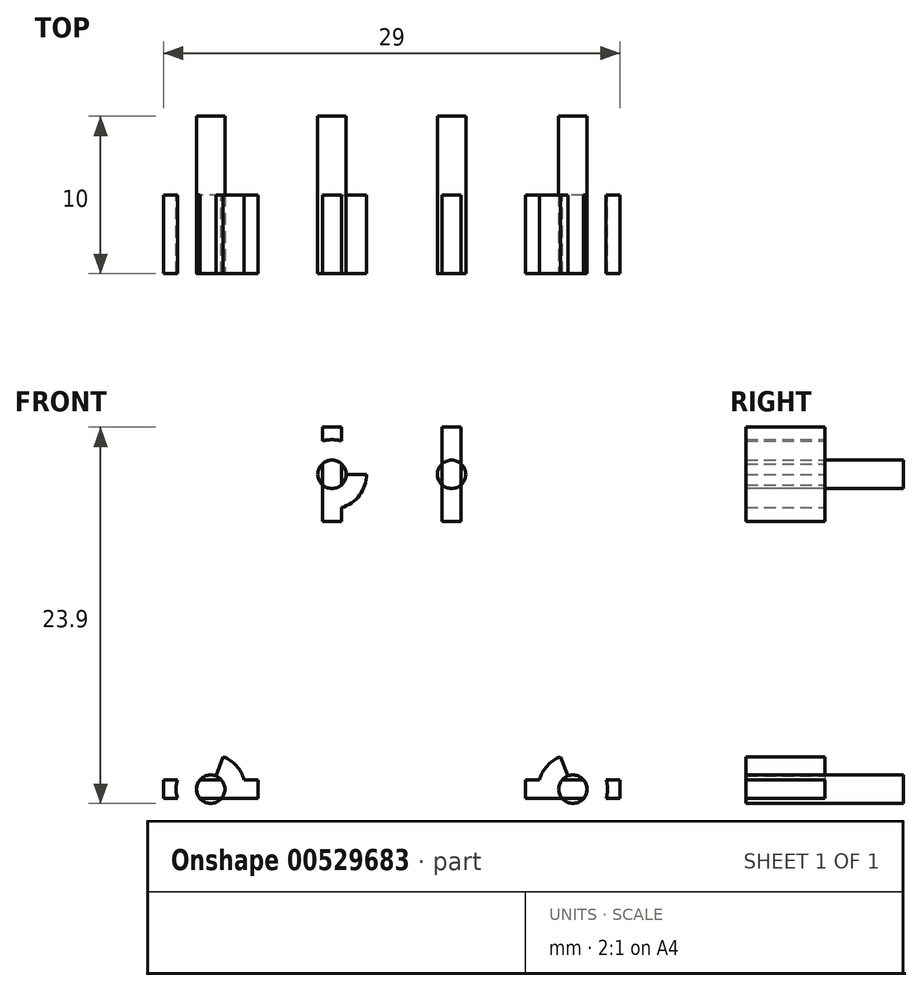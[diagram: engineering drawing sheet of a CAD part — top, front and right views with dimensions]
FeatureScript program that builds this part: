
annotation { "Feature Type Name" : "Feature", "Feature Type Description" : "" }
export const myFeature = defineFeature(function(context is Context, id is Id, definition is map)
    precondition{}
    {
        {
            var Q0;
            Q0=qCreatedBy(makeId("Front.planeOp"),FACE);
            var sketch = newSketch(context, id + "F0", { "sketchPlane" : qUnion([Q0])});
            skLineSegment(sketch, "E0", {"start": v(-3.8, 20) * mm, "end": v(3.8, 20) * mm});
            skLineSegment(sketch, "E1", {"start": v(-11.5, 0) * mm, "end": v(11.5, 0) * mm});
            skLineSegment(sketch, "E2", {"start": v(11.5, 0) * mm, "end": v(3.8, 20) * mm});
            skLineSegment(sketch, "E3", {"start": v(-3.8, 20) * mm, "end": v(-11.5, 0) * mm});
            skCircle(sketch, "E4", {"center": v(-3.8, 20) * mm, "radius": 0.9 * mm});
            skCircle(sketch, "E5", {"center": v(3.8, 20) * mm, "radius": 0.9 * mm});
            skPoint(sketch, "E6", {"position": v(0, 20) * mm});
            skPoint(sketch, "E7", {"position": v(0, 0) * mm});
            skCircle(sketch, "E8", {"center": v(-11.5, 0) * mm, "radius": 0.9 * mm});
            skCircle(sketch, "E9", {"center": v(11.5, 0) * mm, "radius": 0.9 * mm});
            skLineSegment(sketch, "E10.bottom", {"start": v(2.5, 37) * mm, "end": v(-2.5, 37) * mm});
            skLineSegment(sketch, "E10.top", {"start": v(2.5, 30) * mm, "end": v(-2.5, 30) * mm});
            skLineSegment(sketch, "E10.left", {"start": v(2.5, 37) * mm, "end": v(2.5, 30) * mm});
            skLineSegment(sketch, "E10.right", {"start": v(-2.5, 37) * mm, "end": v(-2.5, 30) * mm});
            skPoint(sketch, "E10.middle", {"position": v(0, 33.5) * mm});
            skLineSegment(sketch, "E11.bottom", {"start": v(1.25, 30) * mm, "end": v(-1.25, 30) * mm});
            skLineSegment(sketch, "E11.top", {"start": v(1.25, 35.5) * mm, "end": v(-1.25, 35.5) * mm});
            skLineSegment(sketch, "E11.left", {"start": v(1.25, 30) * mm, "end": v(1.25, 35.5) * mm});
            skLineSegment(sketch, "E11.right", {"start": v(-1.25, 30) * mm, "end": v(-1.25, 35.5) * mm});
            skPoint(sketch, "E11.middle", {"position": v(0, 32.75) * mm});
            skCircle(sketch, "E12", {"center": v(-3.8, 20) * mm, "radius": 2.2 * mm});
            skCircle(sketch, "E13", {"center": v(3.8, 20) * mm, "radius": 2.2 * mm});
            skCircle(sketch, "E14", {"center": v(11.5, 0) * mm, "radius": 2.2 * mm});
            skCircle(sketch, "E15", {"center": v(-11.5, 0) * mm, "radius": 2.2 * mm});
            skLineSegment(sketch, "E16.bottom", {"start": v(-3.2, 17) * mm, "end": v(-4.4, 17) * mm});
            skLineSegment(sketch, "E16.top", {"start": v(-3.2, 23) * mm, "end": v(-4.4, 23) * mm});
            skLineSegment(sketch, "E16.left", {"start": v(-3.2, 17) * mm, "end": v(-3.2, 23) * mm});
            skLineSegment(sketch, "E16.right", {"start": v(-4.4, 17) * mm, "end": v(-4.4, 23) * mm});
            skLineSegment(sketch, "E17.bottom", {"start": v(4.4, 17) * mm, "end": v(3.2, 17) * mm});
            skLineSegment(sketch, "E17.top", {"start": v(4.4, 23) * mm, "end": v(3.2, 23) * mm});
            skLineSegment(sketch, "E17.left", {"start": v(4.4, 17) * mm, "end": v(4.4, 23) * mm});
            skLineSegment(sketch, "E17.right", {"start": v(3.2, 17) * mm, "end": v(3.2, 23) * mm});
            skLineSegment(sketch, "E18.bottom", {"start": v(-8.5, -0.6) * mm, "end": v(-14.5, -0.6) * mm});
            skLineSegment(sketch, "E18.top", {"start": v(-8.5, 0.6) * mm, "end": v(-14.5, 0.6) * mm});
            skLineSegment(sketch, "E18.left", {"start": v(-8.5, -0.6) * mm, "end": v(-8.5, 0.6) * mm});
            skLineSegment(sketch, "E18.right", {"start": v(-14.5, -0.6) * mm, "end": v(-14.5, 0.6) * mm});
            skLineSegment(sketch, "E19.bottom", {"start": v(14.5, -0.6) * mm, "end": v(8.5, -0.6) * mm});
            skLineSegment(sketch, "E19.top", {"start": v(14.5, 0.6) * mm, "end": v(8.5, 0.6) * mm});
            skLineSegment(sketch, "E19.left", {"start": v(14.5, -0.6) * mm, "end": v(14.5, 0.6) * mm});
            skLineSegment(sketch, "E19.right", {"start": v(8.5, -0.6) * mm, "end": v(8.5, 0.6) * mm});
            skSolve(sketch);
        }
        {
            var Q0;
            {var subQ0=sQuery(id+"F0.wireOp",EDGE,"E3");var subQ1=sQuery(id+"F0.wireOp",EDGE,"E0");var subQ2=makeQuery(id+"F0.imprint","INTERSECT",VERTEX,{"derivedFrom":[subQ1,subQ0]});Q0=makeQuery(id+"F0.imprint","IMPRINT",FACE,{"disambiguationData":[TD([[makeQuery(id+"F0.imprint","IMPRINT",EDGE,{"disambiguationData":[TD([[subQ2,-1.0]])],"derivedFrom":subQ1}),1.0]])]});}
            var Q1;
            {var subQ0=sQuery(id+"F0.wireOp",EDGE,"E3");var subQ1=sQuery(id+"F0.wireOp",EDGE,"E0");var subQ2=makeQuery(id+"F0.imprint","INTERSECT",VERTEX,{"derivedFrom":[subQ1,subQ0]});Q1=makeQuery(id+"F0.imprint","IMPRINT",FACE,{"disambiguationData":[TD([[makeQuery(id+"F0.imprint","IMPRINT",EDGE,{"disambiguationData":[TD([[subQ2,-1.0]])],"derivedFrom":subQ1}),-1.0]])]});}
            var Q2;
            {var subQ0=sQuery(id+"F0.wireOp",EDGE,"E2");var subQ1=sQuery(id+"F0.wireOp",EDGE,"E0");var subQ2=makeQuery(id+"F0.imprint","INTERSECT",VERTEX,{"derivedFrom":[subQ1,subQ0]});Q2=makeQuery(id+"F0.imprint","IMPRINT",FACE,{"disambiguationData":[TD([[makeQuery(id+"F0.imprint","IMPRINT",EDGE,{"disambiguationData":[TD([[subQ2,1.0]])],"derivedFrom":subQ1}),1.0]])]});}
            var Q3;
            {var subQ0=sQuery(id+"F0.wireOp",EDGE,"E2");var subQ1=sQuery(id+"F0.wireOp",EDGE,"E0");var subQ2=makeQuery(id+"F0.imprint","INTERSECT",VERTEX,{"derivedFrom":[subQ1,subQ0]});Q3=makeQuery(id+"F0.imprint","IMPRINT",FACE,{"disambiguationData":[TD([[makeQuery(id+"F0.imprint","IMPRINT",EDGE,{"disambiguationData":[TD([[subQ2,1.0]])],"derivedFrom":subQ1}),-1.0]])]});}
            var Q4;
            {var subQ0=sQuery(id+"F0.wireOp",EDGE,"E3");var subQ1=sQuery(id+"F0.wireOp",EDGE,"E1");var subQ2=makeQuery(id+"F0.imprint","INTERSECT",VERTEX,{"derivedFrom":[subQ1,subQ0]});Q4=makeQuery(id+"F0.imprint","IMPRINT",FACE,{"disambiguationData":[TD([[makeQuery(id+"F0.imprint","IMPRINT",EDGE,{"disambiguationData":[TD([[subQ2,-1.0]])],"derivedFrom":subQ1}),-1.0]])]});}
            var Q5;
            {var subQ0=sQuery(id+"F0.wireOp",EDGE,"E3");var subQ1=sQuery(id+"F0.wireOp",EDGE,"E1");var subQ2=makeQuery(id+"F0.imprint","INTERSECT",VERTEX,{"derivedFrom":[subQ1,subQ0]});Q5=makeQuery(id+"F0.imprint","IMPRINT",FACE,{"disambiguationData":[TD([[makeQuery(id+"F0.imprint","IMPRINT",EDGE,{"disambiguationData":[TD([[subQ2,-1.0]])],"derivedFrom":subQ1}),1.0]])]});}
            var Q6;
            {var subQ0=sQuery(id+"F0.wireOp",EDGE,"E2");var subQ1=sQuery(id+"F0.wireOp",EDGE,"E1");var subQ2=makeQuery(id+"F0.imprint","INTERSECT",VERTEX,{"derivedFrom":[subQ1,subQ0]});Q6=makeQuery(id+"F0.imprint","IMPRINT",FACE,{"disambiguationData":[TD([[makeQuery(id+"F0.imprint","IMPRINT",EDGE,{"disambiguationData":[TD([[subQ2,1.0]])],"derivedFrom":subQ1}),-1.0]])]});}
            var Q7;
            {var subQ0=sQuery(id+"F0.wireOp",EDGE,"E2");var subQ1=sQuery(id+"F0.wireOp",EDGE,"E1");var subQ2=makeQuery(id+"F0.imprint","INTERSECT",VERTEX,{"derivedFrom":[subQ1,subQ0]});Q7=makeQuery(id+"F0.imprint","IMPRINT",FACE,{"disambiguationData":[TD([[makeQuery(id+"F0.imprint","IMPRINT",EDGE,{"disambiguationData":[TD([[subQ2,1.0]])],"derivedFrom":subQ1}),1.0]])]});}
            var Q8;
            {var subQ0=sQuery(id+"F0.wireOp",EDGE,"E17.left");var subQ1=sQuery(id+"F0.wireOp",EDGE,"E5");var subQ2=makeQuery(id+"F0.imprint","INTERSECT",VERTEX,{"disambiguationData":[OD(0.0)],"derivedFrom":[subQ1,subQ0]});Q8=makeQuery(id+"F0.imprint","IMPRINT",FACE,{"disambiguationData":[TD([[makeQuery(id+"F0.imprint","IMPRINT",EDGE,{"disambiguationData":[TD([[subQ2,1.0]])],"derivedFrom":subQ1}),1.0]])]});}
            var Q9;
            {var subQ0=sQuery(id+"F0.wireOp",EDGE,"E5");var subQ1=sQuery(id+"F0.wireOp",EDGE,"E0");var subQ2=makeQuery(id+"F0.imprint","INTERSECT",VERTEX,{"derivedFrom":[subQ1,subQ0]});Q9=makeQuery(id+"F0.imprint","IMPRINT",FACE,{"disambiguationData":[TD([[makeQuery(id+"F0.imprint","IMPRINT",EDGE,{"disambiguationData":[TD([[subQ2,-1.0]])],"derivedFrom":subQ1}),1.0]])]});}
            var Q10;
            {var subQ0=sQuery(id+"F0.wireOp",EDGE,"E5");var subQ1=sQuery(id+"F0.wireOp",EDGE,"E0");var subQ2=makeQuery(id+"F0.imprint","INTERSECT",VERTEX,{"derivedFrom":[subQ1,subQ0]});Q10=makeQuery(id+"F0.imprint","IMPRINT",FACE,{"disambiguationData":[TD([[makeQuery(id+"F0.imprint","IMPRINT",EDGE,{"disambiguationData":[TD([[subQ2,-1.0]])],"derivedFrom":subQ1}),-1.0]])]});}
            var Q11;
            {var subQ0=sQuery(id+"F0.wireOp",EDGE,"E16.right");var subQ1=sQuery(id+"F0.wireOp",EDGE,"E4");var subQ2=makeQuery(id+"F0.imprint","INTERSECT",VERTEX,{"disambiguationData":[OD(0.0)],"derivedFrom":[subQ1,subQ0]});Q11=makeQuery(id+"F0.imprint","IMPRINT",FACE,{"disambiguationData":[TD([[makeQuery(id+"F0.imprint","IMPRINT",EDGE,{"disambiguationData":[TD([[subQ2,-1.0]])],"derivedFrom":subQ1}),1.0]])]});}
            var Q12;
            {var subQ0=sQuery(id+"F0.wireOp",EDGE,"E16.left");var subQ1=sQuery(id+"F0.wireOp",EDGE,"E0");var subQ2=makeQuery(id+"F0.imprint","INTERSECT",VERTEX,{"derivedFrom":[subQ1,subQ0]});Q12=makeQuery(id+"F0.imprint","IMPRINT",FACE,{"disambiguationData":[TD([[makeQuery(id+"F0.imprint","IMPRINT",EDGE,{"disambiguationData":[TD([[subQ2,-1.0]])],"derivedFrom":subQ1}),1.0]])]});}
            var Q13;
            {var subQ0=sQuery(id+"F0.wireOp",EDGE,"E16.left");var subQ1=sQuery(id+"F0.wireOp",EDGE,"E0");var subQ2=makeQuery(id+"F0.imprint","INTERSECT",VERTEX,{"derivedFrom":[subQ1,subQ0]});Q13=makeQuery(id+"F0.imprint","IMPRINT",FACE,{"disambiguationData":[TD([[makeQuery(id+"F0.imprint","IMPRINT",EDGE,{"disambiguationData":[TD([[subQ2,-1.0]])],"derivedFrom":subQ1}),-1.0]])]});}
            var Q14;
            {var subQ0=sQuery(id+"F0.wireOp",EDGE,"E18.bottom");var subQ1=sQuery(id+"F0.wireOp",EDGE,"E8");var subQ2=makeQuery(id+"F0.imprint","INTERSECT",VERTEX,{"disambiguationData":[OD(0.0)],"derivedFrom":[subQ1,subQ0]});Q14=makeQuery(id+"F0.imprint","IMPRINT",FACE,{"disambiguationData":[TD([[makeQuery(id+"F0.imprint","IMPRINT",EDGE,{"disambiguationData":[TD([[subQ2,-1.0]])],"derivedFrom":subQ1}),1.0]])]});}
            var Q15;
            {var subQ0=sQuery(id+"F0.wireOp",EDGE,"E8");var subQ1=sQuery(id+"F0.wireOp",EDGE,"E3");var subQ2=makeQuery(id+"F0.imprint","INTERSECT",VERTEX,{"derivedFrom":[subQ1,subQ0]});Q15=makeQuery(id+"F0.imprint","IMPRINT",FACE,{"disambiguationData":[TD([[makeQuery(id+"F0.imprint","IMPRINT",EDGE,{"disambiguationData":[TD([[subQ2,-1.0]])],"derivedFrom":subQ1}),-1.0]])]});}
            var Q16;
            {var subQ0=sQuery(id+"F0.wireOp",EDGE,"E8");var subQ1=sQuery(id+"F0.wireOp",EDGE,"E3");var subQ2=makeQuery(id+"F0.imprint","INTERSECT",VERTEX,{"derivedFrom":[subQ1,subQ0]});Q16=makeQuery(id+"F0.imprint","IMPRINT",FACE,{"disambiguationData":[TD([[makeQuery(id+"F0.imprint","IMPRINT",EDGE,{"disambiguationData":[TD([[subQ2,-1.0]])],"derivedFrom":subQ1}),1.0]])]});}
            var Q17;
            {var subQ0=sQuery(id+"F0.wireOp",EDGE,"E19.top");var subQ1=sQuery(id+"F0.wireOp",EDGE,"E2");var subQ2=makeQuery(id+"F0.imprint","INTERSECT",VERTEX,{"derivedFrom":[subQ1,subQ0]});Q17=makeQuery(id+"F0.imprint","IMPRINT",FACE,{"disambiguationData":[TD([[makeQuery(id+"F0.imprint","IMPRINT",EDGE,{"disambiguationData":[TD([[subQ2,-1.0]])],"derivedFrom":subQ1}),-1.0]])]});}
            var Q18;
            {var subQ0=sQuery(id+"F0.wireOp",EDGE,"E19.top");var subQ1=sQuery(id+"F0.wireOp",EDGE,"E2");var subQ2=makeQuery(id+"F0.imprint","INTERSECT",VERTEX,{"derivedFrom":[subQ1,subQ0]});Q18=makeQuery(id+"F0.imprint","IMPRINT",FACE,{"disambiguationData":[TD([[makeQuery(id+"F0.imprint","IMPRINT",EDGE,{"disambiguationData":[TD([[subQ2,-1.0]])],"derivedFrom":subQ1}),1.0]])]});}
            var Q19;
            {var subQ0=sQuery(id+"F0.wireOp",EDGE,"E19.bottom");var subQ1=sQuery(id+"F0.wireOp",EDGE,"E9");var subQ2=makeQuery(id+"F0.imprint","INTERSECT",VERTEX,{"disambiguationData":[OD(0.0)],"derivedFrom":[subQ1,subQ0]});Q19=makeQuery(id+"F0.imprint","IMPRINT",FACE,{"disambiguationData":[TD([[makeQuery(id+"F0.imprint","IMPRINT",EDGE,{"disambiguationData":[TD([[subQ2,-1.0]])],"derivedFrom":subQ1}),1.0]])]});}
            var Q20;
            Q20=sQuery(id+"F0.wireOp",EDGE,"E4");
            var Q21;
            Q21=sQuery(id+"F0.wireOp",EDGE,"E5");
            extrude(context, id + "F1", {"entities" : qUnion([Q0, Q1, Q2, Q3, Q4, Q5, Q6, Q7, Q8, Q9, Q10, Q11, Q12, Q13, Q14, Q15, Q16, Q17, Q18, Q19]), "surfaceEntities" : qUnion([Q20, Q21]), "oppositeDirection" : true, "depth" : 5 * mm, "offsetDistance" : 25 * mm, "hasSecondDirection" : true, "secondDirectionOppositeDirection" : false, "secondDirectionDepth" : 5 * mm});
        }
        {
            var Q0;
            {var subQ5=sQuery(id+"F0.wireOp",EDGE,"E18.right");Q0=makeQuery(id+"F0.imprint","IMPRINT",FACE,{"disambiguationData":[TD([[makeQuery(id+"F0.imprint","IMPRINT",EDGE,{"derivedFrom":subQ5}),-1.0]])]});}
            var Q1;
            {var subQ0=sQuery(id+"F0.wireOp",EDGE,"E18.top");var subQ1=sQuery(id+"F0.wireOp",EDGE,"E8");var subQ2=makeQuery(id+"F0.imprint","INTERSECT",VERTEX,{"disambiguationData":[OD(1.0)],"derivedFrom":[subQ1,subQ0]});Q1=makeQuery(id+"F0.imprint","IMPRINT",FACE,{"disambiguationData":[TD([[makeQuery(id+"F0.imprint","IMPRINT",EDGE,{"disambiguationData":[TD([[subQ2,-1.0]])],"derivedFrom":subQ1}),-1.0]])]});}
            var Q2;
            {var subQ1=sQuery(id+"F0.wireOp",EDGE,"E1");var subQ8=sQuery(id+"F0.wireOp",EDGE,"E3");var subQ9=makeQuery(id+"F0.imprint","INTERSECT",VERTEX,{"derivedFrom":[subQ1,subQ8]});Q2=makeQuery(id+"F0.imprint","IMPRINT",FACE,{"disambiguationData":[TD([[makeQuery(id+"F0.imprint","IMPRINT",EDGE,{"disambiguationData":[TD([[subQ9,-1.0]])],"derivedFrom":subQ1}),-1.0]])]});}
            var Q3;
            {var subQ0=sQuery(id+"F0.wireOp",EDGE,"E8");var subQ1=sQuery(id+"F0.wireOp",EDGE,"E1");var subQ2=makeQuery(id+"F0.imprint","INTERSECT",VERTEX,{"derivedFrom":[subQ1,subQ0]});Q3=makeQuery(id+"F0.imprint","IMPRINT",FACE,{"disambiguationData":[TD([[makeQuery(id+"F0.imprint","IMPRINT",EDGE,{"disambiguationData":[TD([[subQ2,-1.0]])],"derivedFrom":subQ1}),1.0]])]});}
            var Q4;
            {var subQ0=sQuery(id+"F0.wireOp",EDGE,"E8");var subQ1=sQuery(id+"F0.wireOp",EDGE,"E1");var subQ2=makeQuery(id+"F0.imprint","INTERSECT",VERTEX,{"derivedFrom":[subQ1,subQ0]});Q4=makeQuery(id+"F0.imprint","IMPRINT",FACE,{"disambiguationData":[TD([[makeQuery(id+"F0.imprint","IMPRINT",EDGE,{"disambiguationData":[TD([[subQ2,-1.0]])],"derivedFrom":subQ1}),-1.0]])]});}
            var Q5;
            {var subQ0=sQuery(id+"F0.wireOp",EDGE,"E18.left");var subQ1=sQuery(id+"F0.wireOp",EDGE,"E1");var subQ2=makeQuery(id+"F0.imprint","INTERSECT",VERTEX,{"derivedFrom":[subQ1,subQ0]});Q5=makeQuery(id+"F0.imprint","IMPRINT",FACE,{"disambiguationData":[TD([[makeQuery(id+"F0.imprint","IMPRINT",EDGE,{"disambiguationData":[TD([[subQ2,1.0]])],"derivedFrom":subQ1}),-1.0]])]});}
            var Q6;
            {var subQ0=sQuery(id+"F0.wireOp",EDGE,"E18.left");var subQ1=sQuery(id+"F0.wireOp",EDGE,"E1");var subQ2=makeQuery(id+"F0.imprint","INTERSECT",VERTEX,{"derivedFrom":[subQ1,subQ0]});Q6=makeQuery(id+"F0.imprint","IMPRINT",FACE,{"disambiguationData":[TD([[makeQuery(id+"F0.imprint","IMPRINT",EDGE,{"disambiguationData":[TD([[subQ2,1.0]])],"derivedFrom":subQ1}),1.0]])]});}
            var Q7;
            {var subQ0=sQuery(id+"F0.wireOp",EDGE,"E3");var subQ1=sQuery(id+"F0.wireOp",EDGE,"E1");var subQ2=makeQuery(id+"F0.imprint","INTERSECT",VERTEX,{"derivedFrom":[subQ1,subQ0]});Q7=makeQuery(id+"F0.imprint","IMPRINT",FACE,{"disambiguationData":[TD([[makeQuery(id+"F0.imprint","IMPRINT",EDGE,{"disambiguationData":[TD([[subQ2,-1.0]])],"derivedFrom":subQ1}),1.0]])]});}
            var Q8;
            {var subQ0=sQuery(id+"F0.wireOp",EDGE,"E19.right");var subQ1=sQuery(id+"F0.wireOp",EDGE,"E1");var subQ2=makeQuery(id+"F0.imprint","INTERSECT",VERTEX,{"derivedFrom":[subQ1,subQ0]});Q8=makeQuery(id+"F0.imprint","IMPRINT",FACE,{"disambiguationData":[TD([[makeQuery(id+"F0.imprint","IMPRINT",EDGE,{"disambiguationData":[TD([[subQ2,-1.0]])],"derivedFrom":subQ1}),1.0]])]});}
            var Q9;
            {var subQ0=sQuery(id+"F0.wireOp",EDGE,"E19.right");var subQ1=sQuery(id+"F0.wireOp",EDGE,"E1");var subQ2=makeQuery(id+"F0.imprint","INTERSECT",VERTEX,{"derivedFrom":[subQ1,subQ0]});Q9=makeQuery(id+"F0.imprint","IMPRINT",FACE,{"disambiguationData":[TD([[makeQuery(id+"F0.imprint","IMPRINT",EDGE,{"disambiguationData":[TD([[subQ2,-1.0]])],"derivedFrom":subQ1}),-1.0]])]});}
            var Q10;
            {var subQ0=sQuery(id+"F0.wireOp",EDGE,"E14");var subQ1=sQuery(id+"F0.wireOp",EDGE,"E1");var subQ2=makeQuery(id+"F0.imprint","INTERSECT",VERTEX,{"derivedFrom":[subQ1,subQ0]});Q10=makeQuery(id+"F0.imprint","IMPRINT",FACE,{"disambiguationData":[TD([[makeQuery(id+"F0.imprint","IMPRINT",EDGE,{"disambiguationData":[TD([[subQ2,-1.0]])],"derivedFrom":subQ1}),-1.0]])]});}
            var Q11;
            {var subQ0=sQuery(id+"F0.wireOp",EDGE,"E14");var subQ1=sQuery(id+"F0.wireOp",EDGE,"E1");var subQ2=makeQuery(id+"F0.imprint","INTERSECT",VERTEX,{"derivedFrom":[subQ1,subQ0]});Q11=makeQuery(id+"F0.imprint","IMPRINT",FACE,{"disambiguationData":[TD([[makeQuery(id+"F0.imprint","IMPRINT",EDGE,{"disambiguationData":[TD([[subQ2,-1.0]])],"derivedFrom":subQ1}),1.0]])]});}
            var Q12;
            {var subQ0=sQuery(id+"F0.wireOp",EDGE,"E2");var subQ1=sQuery(id+"F0.wireOp",EDGE,"E1");var subQ2=makeQuery(id+"F0.imprint","INTERSECT",VERTEX,{"derivedFrom":[subQ1,subQ0]});Q12=makeQuery(id+"F0.imprint","IMPRINT",FACE,{"disambiguationData":[TD([[makeQuery(id+"F0.imprint","IMPRINT",EDGE,{"disambiguationData":[TD([[subQ2,1.0]])],"derivedFrom":subQ1}),1.0]])]});}
            var Q13;
            {var subQ5=sQuery(id+"F0.wireOp",EDGE,"E1");var subQ8=sQuery(id+"F0.wireOp",EDGE,"E2");var subQ9=makeQuery(id+"F0.imprint","INTERSECT",VERTEX,{"derivedFrom":[subQ5,subQ8]});Q13=makeQuery(id+"F0.imprint","IMPRINT",FACE,{"disambiguationData":[TD([[makeQuery(id+"F0.imprint","IMPRINT",EDGE,{"disambiguationData":[TD([[subQ9,1.0]])],"derivedFrom":subQ5}),-1.0]])]});}
            var Q14;
            {var subQ0=sQuery(id+"F0.wireOp",EDGE,"E19.top");var subQ1=sQuery(id+"F0.wireOp",EDGE,"E9");var subQ2=makeQuery(id+"F0.imprint","INTERSECT",VERTEX,{"disambiguationData":[OD(0.0)],"derivedFrom":[subQ1,subQ0]});Q14=makeQuery(id+"F0.imprint","IMPRINT",FACE,{"disambiguationData":[TD([[makeQuery(id+"F0.imprint","IMPRINT",EDGE,{"disambiguationData":[TD([[subQ2,1.0]])],"derivedFrom":subQ1}),-1.0]])]});}
            var Q15;
            {var subQ5=sQuery(id+"F0.wireOp",EDGE,"E19.left");Q15=makeQuery(id+"F0.imprint","IMPRINT",FACE,{"disambiguationData":[TD([[makeQuery(id+"F0.imprint","IMPRINT",EDGE,{"derivedFrom":subQ5}),1.0]])]});}
            var Q16;
            {var subQ5=sQuery(id+"F0.wireOp",EDGE,"E17.bottom");Q16=makeQuery(id+"F0.imprint","IMPRINT",FACE,{"disambiguationData":[TD([[makeQuery(id+"F0.imprint","IMPRINT",EDGE,{"derivedFrom":subQ5}),-1.0]])]});}
            var Q17;
            {var subQ3=sQuery(id+"F0.wireOp",EDGE,"E17.left");var subQ6=sQuery(id+"F0.wireOp",EDGE,"E2");var subQ9=makeQuery(id+"F0.imprint","INTERSECT",VERTEX,{"derivedFrom":[subQ6,subQ3]});Q17=makeQuery(id+"F0.imprint","IMPRINT",FACE,{"disambiguationData":[TD([[makeQuery(id+"F0.imprint","IMPRINT",EDGE,{"disambiguationData":[TD([[subQ9,-1.0]])],"derivedFrom":subQ6}),1.0]])]});}
            var Q18;
            {var subQ0=sQuery(id+"F0.wireOp",EDGE,"E2");var subQ1=sQuery(id+"F0.wireOp",EDGE,"E0");var subQ2=makeQuery(id+"F0.imprint","INTERSECT",VERTEX,{"derivedFrom":[subQ1,subQ0]});Q18=makeQuery(id+"F0.imprint","IMPRINT",FACE,{"disambiguationData":[TD([[makeQuery(id+"F0.imprint","IMPRINT",EDGE,{"disambiguationData":[TD([[subQ2,1.0]])],"derivedFrom":subQ1}),-1.0]])]});}
            var Q19;
            {var subQ0=sQuery(id+"F0.wireOp",EDGE,"E17.left");var subQ1=sQuery(id+"F0.wireOp",EDGE,"E2");var subQ2=makeQuery(id+"F0.imprint","INTERSECT",VERTEX,{"derivedFrom":[subQ1,subQ0]});Q19=makeQuery(id+"F0.imprint","IMPRINT",FACE,{"disambiguationData":[TD([[makeQuery(id+"F0.imprint","IMPRINT",EDGE,{"disambiguationData":[TD([[subQ2,-1.0]])],"derivedFrom":subQ1}),-1.0]])]});}
            var Q20;
            {var subQ1=sQuery(id+"F0.wireOp",EDGE,"E2");var subQ8=sQuery(id+"F0.wireOp",EDGE,"E0");var subQ9=makeQuery(id+"F0.imprint","INTERSECT",VERTEX,{"derivedFrom":[subQ8,subQ1]});Q20=makeQuery(id+"F0.imprint","IMPRINT",FACE,{"disambiguationData":[TD([[makeQuery(id+"F0.imprint","IMPRINT",EDGE,{"disambiguationData":[TD([[subQ9,1.0]])],"derivedFrom":subQ8}),1.0]])]});}
            var Q21;
            {var subQ0=sQuery(id+"F0.wireOp",EDGE,"E17.right");var subQ1=sQuery(id+"F0.wireOp",EDGE,"E5");var subQ2=makeQuery(id+"F0.imprint","INTERSECT",VERTEX,{"disambiguationData":[OD(0.0)],"derivedFrom":[subQ1,subQ0]});Q21=makeQuery(id+"F0.imprint","IMPRINT",FACE,{"disambiguationData":[TD([[makeQuery(id+"F0.imprint","IMPRINT",EDGE,{"disambiguationData":[TD([[subQ2,1.0]])],"derivedFrom":subQ1}),-1.0]])]});}
            var Q22;
            {var subQ5=sQuery(id+"F0.wireOp",EDGE,"E17.top");Q22=makeQuery(id+"F0.imprint","IMPRINT",FACE,{"disambiguationData":[TD([[makeQuery(id+"F0.imprint","IMPRINT",EDGE,{"derivedFrom":subQ5}),1.0]])]});}
            var Q23;
            {var subQ1=sQuery(id+"F0.wireOp",EDGE,"E4");var subQ5=sQuery(id+"F0.wireOp",EDGE,"E3");var subQ6=makeQuery(id+"F0.imprint","INTERSECT",VERTEX,{"derivedFrom":[subQ5,subQ1]});Q23=makeQuery(id+"F0.imprint","IMPRINT",FACE,{"disambiguationData":[TD([[makeQuery(id+"F0.imprint","IMPRINT",EDGE,{"disambiguationData":[TD([[subQ6,-1.0]])],"derivedFrom":subQ5}),1.0]])]});}
            var Q24;
            {var subQ5=sQuery(id+"F0.wireOp",EDGE,"E16.bottom");Q24=makeQuery(id+"F0.imprint","IMPRINT",FACE,{"disambiguationData":[TD([[makeQuery(id+"F0.imprint","IMPRINT",EDGE,{"derivedFrom":subQ5}),-1.0]])]});}
            var Q25;
            {var subQ0=sQuery(id+"F0.wireOp",EDGE,"E4");var subQ1=sQuery(id+"F0.wireOp",EDGE,"E3");var subQ2=makeQuery(id+"F0.imprint","INTERSECT",VERTEX,{"derivedFrom":[subQ1,subQ0]});Q25=makeQuery(id+"F0.imprint","IMPRINT",FACE,{"disambiguationData":[TD([[makeQuery(id+"F0.imprint","IMPRINT",EDGE,{"disambiguationData":[TD([[subQ2,-1.0]])],"derivedFrom":subQ1}),-1.0]])]});}
            var Q26;
            {var subQ5=sQuery(id+"F0.wireOp",EDGE,"E3");var subQ8=sQuery(id+"F0.wireOp",EDGE,"E0");var subQ9=makeQuery(id+"F0.imprint","INTERSECT",VERTEX,{"derivedFrom":[subQ8,subQ5]});Q26=makeQuery(id+"F0.imprint","IMPRINT",FACE,{"disambiguationData":[TD([[makeQuery(id+"F0.imprint","IMPRINT",EDGE,{"disambiguationData":[TD([[subQ9,-1.0]])],"derivedFrom":subQ8}),1.0]])]});}
            var Q27;
            {var subQ0=sQuery(id+"F0.wireOp",EDGE,"E3");var subQ1=sQuery(id+"F0.wireOp",EDGE,"E0");var subQ2=makeQuery(id+"F0.imprint","INTERSECT",VERTEX,{"derivedFrom":[subQ1,subQ0]});Q27=makeQuery(id+"F0.imprint","IMPRINT",FACE,{"disambiguationData":[TD([[makeQuery(id+"F0.imprint","IMPRINT",EDGE,{"disambiguationData":[TD([[subQ2,-1.0]])],"derivedFrom":subQ1}),-1.0]])]});}
            var Q28;
            {var subQ0=sQuery(id+"F0.wireOp",EDGE,"E16.left");var subQ1=sQuery(id+"F0.wireOp",EDGE,"E4");var subQ2=makeQuery(id+"F0.imprint","INTERSECT",VERTEX,{"disambiguationData":[OD(0.0)],"derivedFrom":[subQ1,subQ0]});Q28=makeQuery(id+"F0.imprint","IMPRINT",FACE,{"disambiguationData":[TD([[makeQuery(id+"F0.imprint","IMPRINT",EDGE,{"disambiguationData":[TD([[subQ2,-1.0]])],"derivedFrom":subQ1}),-1.0]])]});}
            var Q29;
            {var subQ5=sQuery(id+"F0.wireOp",EDGE,"E16.top");Q29=makeQuery(id+"F0.imprint","IMPRINT",FACE,{"disambiguationData":[TD([[makeQuery(id+"F0.imprint","IMPRINT",EDGE,{"derivedFrom":subQ5}),1.0]])]});}
            extrude(context, id + "F2", {"entities" : qUnion([Q0, Q1, Q2, Q3, Q4, Q5, Q6, Q7, Q8, Q9, Q10, Q11, Q12, Q13, Q14, Q15, Q16, Q17, Q18, Q19, Q20, Q21, Q22, Q23, Q24, Q25, Q26, Q27, Q28, Q29]), "depth" : 5 * mm, "offsetDistance" : 25 * mm});
        }
    });
